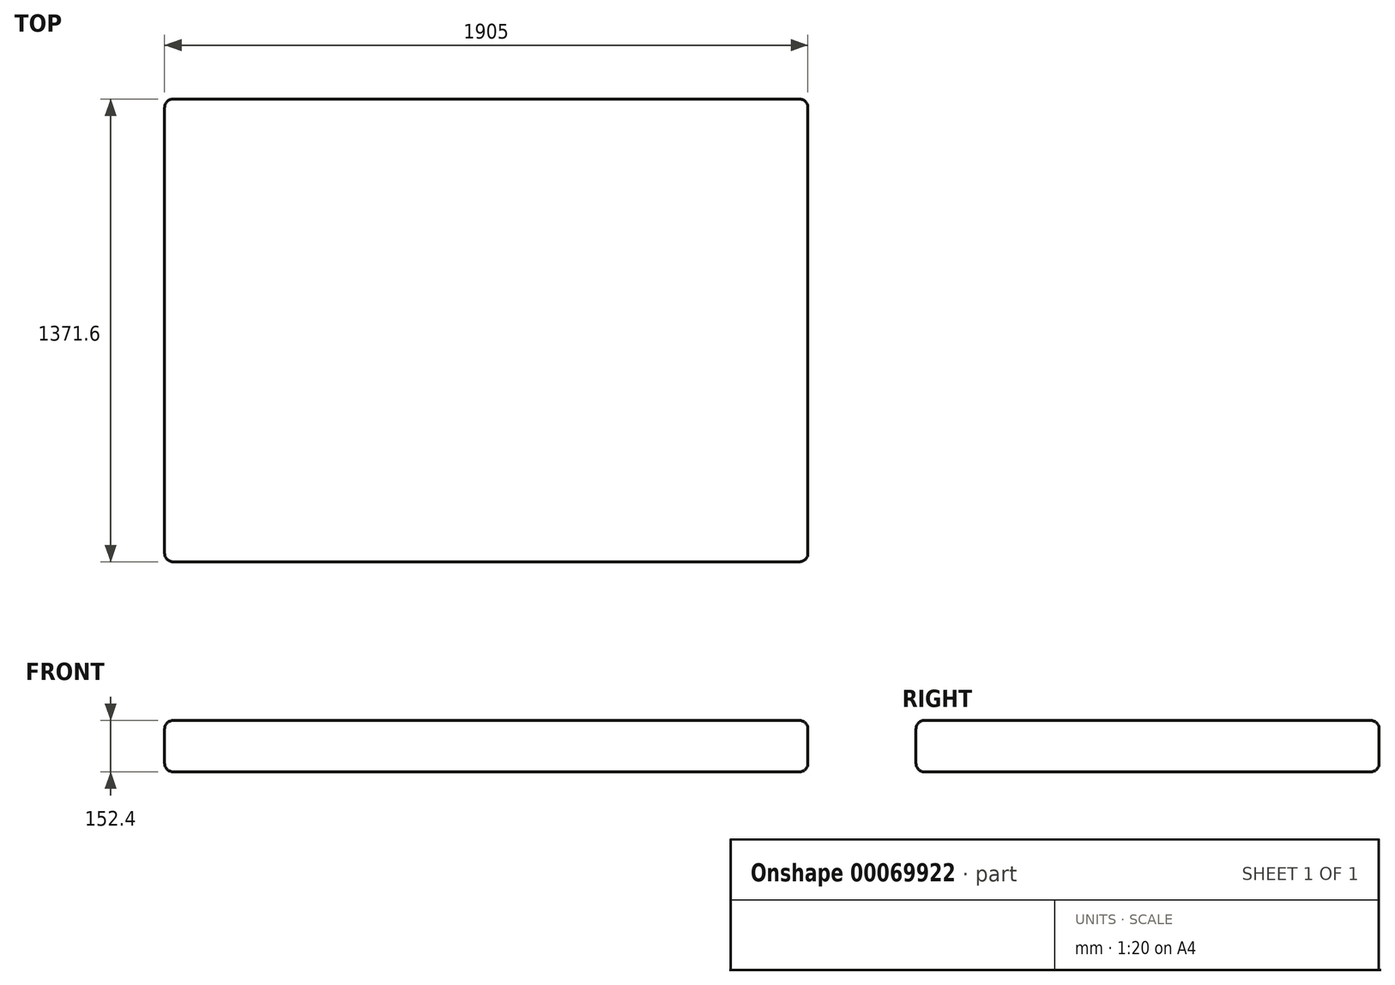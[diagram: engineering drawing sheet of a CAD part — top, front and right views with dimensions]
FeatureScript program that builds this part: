
annotation { "Feature Type Name" : "Feature", "Feature Type Description" : "" }
export const myFeature = defineFeature(function(context is Context, id is Id, definition is map)
    precondition{}
    {
        {
            var Q0;
            Q0=qCreatedBy(makeId("Top.planeOp"),FACE);
            var sketch = newSketch(context, id + "F0", { "sketchPlane" : qUnion([Q0])});
            skLineSegment(sketch, "E0.bottom", {"start": v(952.5, -685.8) * mm, "end": v(-952.5, -685.8) * mm});
            skLineSegment(sketch, "E0.top", {"start": v(952.5, 685.8) * mm, "end": v(-952.5, 685.8) * mm});
            skLineSegment(sketch, "E0.left", {"start": v(952.5, -685.8) * mm, "end": v(952.5, 685.8) * mm});
            skLineSegment(sketch, "E0.right", {"start": v(-952.5, -685.8) * mm, "end": v(-952.5, 685.8) * mm});
            skPoint(sketch, "E0.middle", {"position": v(0, 0) * mm});
            skSolve(sketch);
        }
        {
            var Q0;
            Q0 = qSketchRegion(id + "F0", true);
            extrude(context, id + "F1", {"entities" : qUnion([Q0]), "depth" : 152.4 * mm});
        }
        {
            var Q0;
            Q0=makeQuery(id+"F1.opExtrude","CAP_FACE",FACE,{"disambiguationData":[OSD([sQuery(id+"F0.wireOp",EDGE,"E0.bottom"),sQuery(id+"F0.wireOp",EDGE,"E0.top"),sQuery(id+"F0.wireOp",EDGE,"E0.left"),sQuery(id+"F0.wireOp",EDGE,"E0.right")])],"isStart":false});
            var Q1;
            Q1=makeQuery(id+"F1.opExtrude","CAP_FACE",FACE,{"disambiguationData":[OSD([sQuery(id+"F0.wireOp",EDGE,"E0.bottom"),sQuery(id+"F0.wireOp",EDGE,"E0.top"),sQuery(id+"F0.wireOp",EDGE,"E0.left"),sQuery(id+"F0.wireOp",EDGE,"E0.right")])],"isStart":true});
            var Q2;
            Q2=makeQuery(id+"F1.opExtrude","SWEPT_EDGE",EDGE,{"disambiguationData":[OSD([sQuery(id+"F0.wireOp",EDGE,"E0.bottom"),sQuery(id+"F0.wireOp",EDGE,"E0.left")])]});
            var Q3;
            Q3=makeQuery(id+"F1.opExtrude","SWEPT_EDGE",EDGE,{"disambiguationData":[OSD([sQuery(id+"F0.wireOp",EDGE,"E0.bottom"),sQuery(id+"F0.wireOp",EDGE,"E0.right")])]});
            var Q4;
            Q4=makeQuery(id+"F1.opExtrude","SWEPT_EDGE",EDGE,{"disambiguationData":[OSD([sQuery(id+"F0.wireOp",EDGE,"E0.top"),sQuery(id+"F0.wireOp",EDGE,"E0.left")])]});
            var Q5;
            Q5=makeQuery(id+"F1.opExtrude","SWEPT_EDGE",EDGE,{"disambiguationData":[OSD([sQuery(id+"F0.wireOp",EDGE,"E0.top"),sQuery(id+"F0.wireOp",EDGE,"E0.right")])]});
            fillet(context, id + "F2", {"entities" : qUnion([Q0, Q1, Q2, Q3, Q4, Q5]), "radius" : 25.4 * mm, "tangentPropagation" : true, "allowEdgeOverflow" : false});
        }
    });
